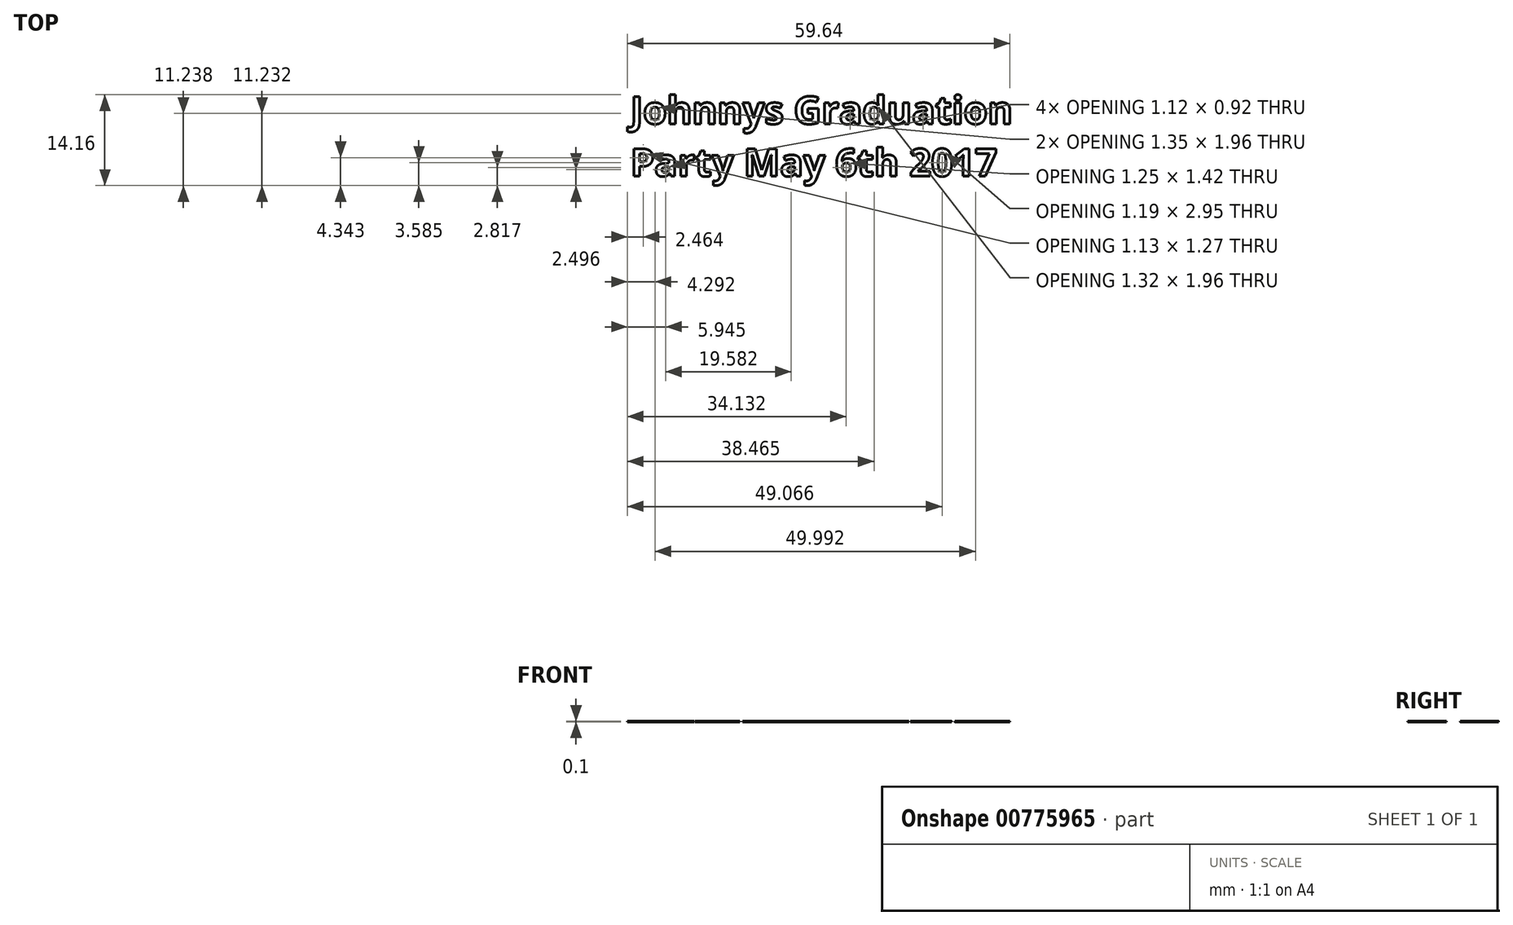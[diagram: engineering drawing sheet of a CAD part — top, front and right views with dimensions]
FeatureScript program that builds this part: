
annotation { "Feature Type Name" : "Feature", "Feature Type Description" : "" }
export const myFeature = defineFeature(function(context is Context, id is Id, definition is map)
    precondition{}
    {
        {
            var Q0;
            Q0=qCreatedBy(makeId("Top.planeOp"),FACE);
            var sketch = newSketch(context, id + "F0", { "sketchPlane" : qUnion([Q0])});
            skLineSegment(sketch, "E0.bottom", {"start": v(0, 0) * mm, "end": v(70, 0) * mm, "construction": true});
            skLineSegment(sketch, "E0.top", {"start": v(0, 100) * mm, "end": v(70, 100) * mm, "construction": true});
            skLineSegment(sketch, "E0.left", {"start": v(0, 0) * mm, "end": v(0, 100) * mm, "construction": true});
            skLineSegment(sketch, "E0.right", {"start": v(70, 0) * mm, "end": v(70, 100) * mm, "construction": true});
            skText(sketch, "E1", { "text": "Johnnys Graduation \nParty May 6th 2017", "fontName": "OpenSans-Bold.ttf"});
            const initialGuessF0  = {"E1": [0.005, 0.07909, 1, 0, 0.00432]};
            skSetInitialGuess(sketch, initialGuessF0);
            skSolve(sketch);
        }
        {
            var Q0;
            Q0 = qSketchRegion(id + "F0", true);
            extrude(context, id + "F1", {"entities" : qUnion([Q0]), "depth" : .1 * mm, "offsetDistance" : 25 * mm});
        }
    });
